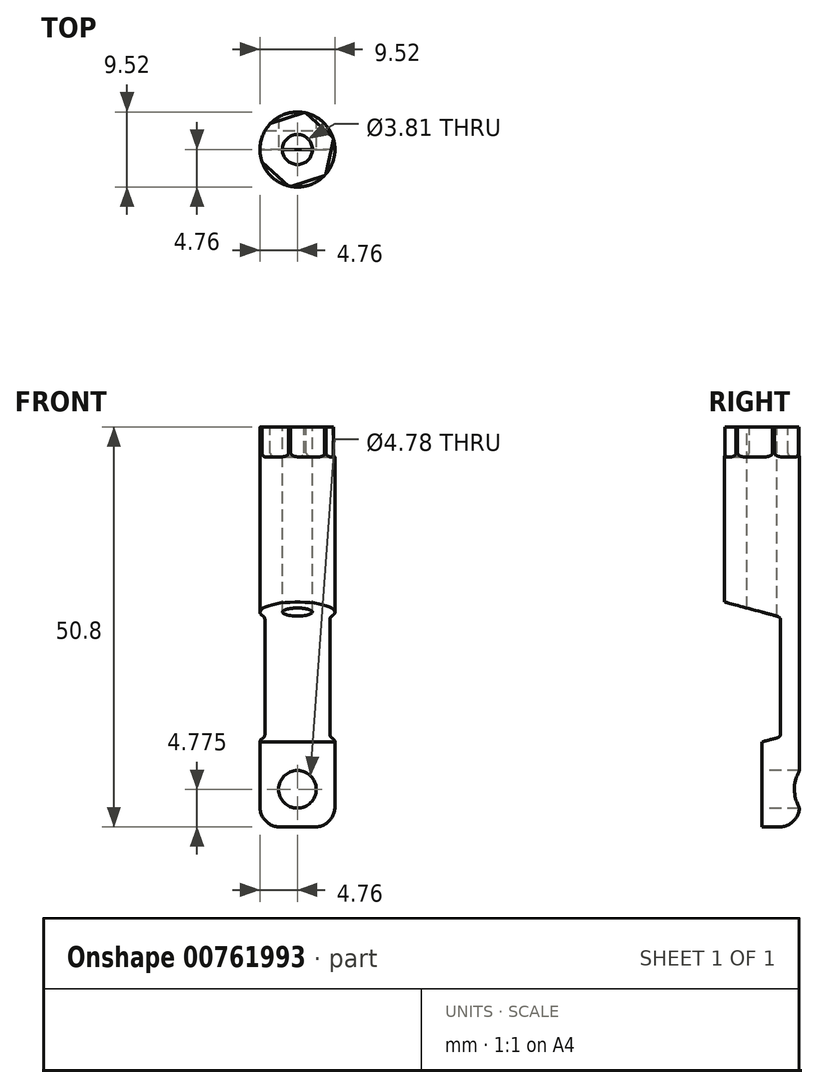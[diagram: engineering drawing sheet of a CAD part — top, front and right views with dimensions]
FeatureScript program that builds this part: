
annotation { "Feature Type Name" : "Feature", "Feature Type Description" : "" }
export const myFeature = defineFeature(function(context is Context, id is Id, definition is map)
    precondition{}
    {
        {
            var Q0;
            Q0=qCreatedBy(makeId("Top.planeOp"),FACE);
            var sketch = newSketch(context, id + "F0", { "sketchPlane" : qUnion([Q0])});
            skCircle(sketch, "E0", {"center": v(0, 0) * mm, "radius": 4.76 * mm});
            skSolve(sketch);
        }
        {
            var Q0;
            Q0=makeQuery(id+"F0.imprint","IMPRINT",FACE,{"disambiguationData":[TD([[makeQuery(id+"F0.imprint","IMPRINT",EDGE,{"derivedFrom":sQuery(id+"F0.wireOp",EDGE,"E0")}),1.0]])]});
            extrude(context, id + "F1", {"entities" : qUnion([Q0]), "depth" : 50.8 * mm, "offsetDistance" : 25.4 * mm});
        }
        {
            var Q0;
            Q0=qCreatedBy(makeId("Front.planeOp"),FACE);
            cPlane(context, id + "F2", {"entities" : qUnion([Q0]), "cplaneType" : CPlaneType.OFFSET, "offset" : 4.76 * mm, "width" : 152.4 * mm, "height" : 152.4 * mm});
        }
        {
            var Q0;
            Q0=qCreatedBy(id+"F2.planeOp",FACE);
            var sketch = newSketch(context, id + "F3", { "sketchPlane" : qUnion([Q0])});
            skLineSegment(sketch, "E1.bottom", {"start": v(-7.62, 9.53) * mm, "end": v(7.62, 9.53) * mm});
            skLineSegment(sketch, "E1.top", {"start": v(-7.62, 28.57) * mm, "end": v(7.62, 28.57) * mm});
            skLineSegment(sketch, "E1.left", {"start": v(-7.62, 9.53) * mm, "end": v(-7.62, 28.57) * mm});
            skLineSegment(sketch, "E1.right", {"start": v(7.62, 9.53) * mm, "end": v(7.62, 28.57) * mm});
            skSolve(sketch);
        }
        {
            var Q0;
            Q0 = qSketchRegion(id + "F3", true);
            extrude(context, id + "F4", {"entities" : qUnion([Q0]), "operationType" : NewBodyOperationType.REMOVE, "oppositeDirection" : true, "depth" : 7.14 * mm, "offsetDistance" : 25.4 * mm, "hasDraft" : true, "draftAngle" : 15 * degree, "draftPullDirection" : true});
        }
        {
            var Q0;
            Q0=qCreatedBy(id+"F2.planeOp",FACE);
            var sketch = newSketch(context, id + "F5", { "sketchPlane" : qUnion([Q0])});
            skLineSegment(sketch, "E2.bottom", {"start": v(-8.92, 12.6) * mm, "end": v(11.04, 12.6) * mm});
            skLineSegment(sketch, "E2.top", {"start": v(-8.92, -5.6) * mm, "end": v(11.04, -5.6) * mm});
            skLineSegment(sketch, "E2.left", {"start": v(-8.92, 12.6) * mm, "end": v(-8.92, -5.6) * mm});
            skLineSegment(sketch, "E2.right", {"start": v(11.04, 12.6) * mm, "end": v(11.04, -5.6) * mm});
            skSolve(sketch);
        }
        {
            var Q0;
            Q0 = qSketchRegion(id + "F5", true);
            extrude(context, id + "F6", {"entities" : qUnion([Q0]), "operationType" : NewBodyOperationType.REMOVE, "oppositeDirection" : true, "depth" : 4.78 * mm, "offsetDistance" : 25.4 * mm});
        }
        {
            var Q0;
            Q0=makeQuery(id+"F1.opExtrude","CAP_EDGE",EDGE,{"disambiguationData":[OSD([sQuery(id+"F0.wireOp",EDGE,"E0")])],"isStart":true});
            fillet(context, id + "F7", {"entities" : qUnion([Q0]), "radius" : 2.54 * mm, "tangentPropagation" : true, "allowEdgeOverflow" : false});
        }
        {
            var Q0;
            Q0=makeQuery(id+"F6.boolean.opBoolean","COPY",FACE,{"derivedFrom":makeQuery(id+"F6.opExtrude","CAP_FACE",FACE,{"disambiguationData":[OSD([sQuery(id+"F5.wireOp",EDGE,"E2.bottom"),sQuery(id+"F5.wireOp",EDGE,"E2.top"),sQuery(id+"F5.wireOp",EDGE,"E2.left"),sQuery(id+"F5.wireOp",EDGE,"E2.right")])],"isStart":false})});
            var sketch = newSketch(context, id + "F8", { "sketchPlane" : qUnion([Q0])});
            skCircle(sketch, "E3", {"center": v(0, 4.78) * mm, "radius": 2.39 * mm});
            skSolve(sketch);
        }
        {
            var Q0;
            Q0=makeQuery(id+"F8.imprint","IMPRINT",FACE,{"disambiguationData":[TD([[makeQuery(id+"F8.imprint","IMPRINT",EDGE,{"derivedFrom":sQuery(id+"F8.wireOp",EDGE,"E3")}),1.0]])]});
            extrude(context, id + "F9", {"entities" : qUnion([Q0]), "operationType" : NewBodyOperationType.REMOVE, "oppositeDirection" : true, "depth" : 25.4 * mm, "offsetDistance" : 25.4 * mm});
        }
        {
            var Q0;
            Q0=makeQuery(id+"F1.opExtrude","CAP_FACE",FACE,{"disambiguationData":[OSD([sQuery(id+"F0.wireOp",EDGE,"E0")])],"isStart":false});
            var sketch = newSketch(context, id + "F10", { "sketchPlane" : qUnion([Q0])});
            skCircle(sketch, "E4", {"center": v(0, 0) * mm, "radius": 1.9 * mm});
            skSolve(sketch);
        }
        {
            var Q0;
            Q0 = qSketchRegion(id + "F10", true);
            extrude(context, id + "F11", {"entities" : qUnion([Q0]), "operationType" : NewBodyOperationType.REMOVE, "oppositeDirection" : true, "depth" : 25.4 * mm, "offsetDistance" : 25.4 * mm});
        }
        {
            var Q0;
            Q0=makeQuery(id+"F1.opExtrude","CAP_FACE",FACE,{"disambiguationData":[OSD([sQuery(id+"F0.wireOp",EDGE,"E0")])],"isStart":false});
            var sketch = newSketch(context, id + "F12", { "sketchPlane" : qUnion([Q0])});
            skCircle(sketch, "E5.cCircle", {"center": v(0, 0) * mm, "radius": 4.84 * mm, "construction": true});
            skLineSegment(sketch, "E5.0", {"start": v(3.6, -3.23) * mm, "end": v(-1, -4.73) * mm});
            skLineSegment(sketch, "E5.1", {"start": v(-1, -4.73) * mm, "end": v(-4.6, -1.5) * mm});
            skLineSegment(sketch, "E5.2", {"start": v(-4.6, -1.5) * mm, "end": v(-3.63, 3.08) * mm});
            skLineSegment(sketch, "E5.3", {"start": v(-3.6, 3.23) * mm, "end": v(1, 4.73) * mm});
            skLineSegment(sketch, "E5.4", {"start": v(1, 4.73) * mm, "end": v(4.6, 1.5) * mm});
            skLineSegment(sketch, "E5.5", {"start": v(4.6, 1.5) * mm, "end": v(3.6, -3.23) * mm});
            skLineSegment(sketch, "E6", {"start": v(-4.6, -1.5) * mm, "end": v(-3.6, 3.23) * mm});
            skSolve(sketch);
        }
        {
            var Q0;
            {var subQ0=sQuery(id+"F12.wireOp",EDGE,"E6");var subQ1=makeQuery(id+"F12.imprint","IMPRINT",VERTEX,{"derivedFrom":subQ0});Q0=makeQuery(id+"F12.imprint","IMPRINT",FACE,{"disambiguationData":[TD([[makeQuery(id+"F12.imprint","IMPRINT",EDGE,{"disambiguationData":[TD([[subQ1,1.0]])],"derivedFrom":subQ0}),1.0]])]});}
            var Q1;
            {var subQ0=sQuery(id+"F12.wireOp",EDGE,"E5.1");var subQ1=makeQuery(id+"F1.opExtrude","CAP_EDGE",EDGE,{"disambiguationData":[OSD([sQuery(id+"F0.wireOp",EDGE,"E0")])],"isStart":false});var subQ2=makeQuery(id+"F12.imprint","INTERSECT",VERTEX,{"disambiguationData":[OD(0.0)],"derivedFrom":[subQ1,subQ0]});Q1=makeQuery(id+"F12.imprint","IMPRINT",FACE,{"disambiguationData":[TD([[makeQuery(id+"F12.imprint","IMPRINT",EDGE,{"disambiguationData":[TD([[subQ2,-1.0]])],"derivedFrom":subQ0}),1.0]])]});}
            var Q2;
            {var subQ0=sQuery(id+"F12.wireOp",EDGE,"E5.3");var subQ1=makeQuery(id+"F1.opExtrude","CAP_EDGE",EDGE,{"disambiguationData":[OSD([sQuery(id+"F0.wireOp",EDGE,"E0")])],"isStart":false});var subQ2=makeQuery(id+"F12.imprint","INTERSECT",VERTEX,{"disambiguationData":[OD(0.0)],"derivedFrom":[subQ1,subQ0]});Q2=makeQuery(id+"F12.imprint","IMPRINT",FACE,{"disambiguationData":[TD([[makeQuery(id+"F12.imprint","IMPRINT",EDGE,{"disambiguationData":[TD([[subQ2,-1.0]])],"derivedFrom":subQ0}),1.0]])]});}
            var Q3;
            {var subQ0=sQuery(id+"F12.wireOp",EDGE,"E5.4");var subQ1=makeQuery(id+"F1.opExtrude","CAP_EDGE",EDGE,{"disambiguationData":[OSD([sQuery(id+"F0.wireOp",EDGE,"E0")])],"isStart":false});var subQ2=makeQuery(id+"F12.imprint","INTERSECT",VERTEX,{"disambiguationData":[OD(0.0)],"derivedFrom":[subQ1,subQ0]});Q3=makeQuery(id+"F12.imprint","IMPRINT",FACE,{"disambiguationData":[TD([[makeQuery(id+"F12.imprint","IMPRINT",EDGE,{"disambiguationData":[TD([[subQ2,-1.0]])],"derivedFrom":subQ0}),1.0]])]});}
            var Q4;
            {var subQ0=sQuery(id+"F12.wireOp",EDGE,"E5.5");var subQ1=makeQuery(id+"F1.opExtrude","CAP_EDGE",EDGE,{"disambiguationData":[OSD([sQuery(id+"F0.wireOp",EDGE,"E0")])],"isStart":false});var subQ2=makeQuery(id+"F12.imprint","INTERSECT",VERTEX,{"disambiguationData":[OD(0.0)],"derivedFrom":[subQ1,subQ0]});Q4=makeQuery(id+"F12.imprint","IMPRINT",FACE,{"disambiguationData":[TD([[makeQuery(id+"F12.imprint","IMPRINT",EDGE,{"disambiguationData":[TD([[subQ2,-1.0]])],"derivedFrom":subQ0}),1.0]])]});}
            var Q5;
            {var subQ0=sQuery(id+"F12.wireOp",EDGE,"E5.0");var subQ1=makeQuery(id+"F1.opExtrude","CAP_EDGE",EDGE,{"disambiguationData":[OSD([sQuery(id+"F0.wireOp",EDGE,"E0")])],"isStart":false});var subQ2=makeQuery(id+"F12.imprint","INTERSECT",VERTEX,{"disambiguationData":[OD(0.0)],"derivedFrom":[subQ1,subQ0]});Q5=makeQuery(id+"F12.imprint","IMPRINT",FACE,{"disambiguationData":[TD([[makeQuery(id+"F12.imprint","IMPRINT",EDGE,{"disambiguationData":[TD([[subQ2,-1.0]])],"derivedFrom":subQ0}),1.0]])]});}
            extrude(context, id + "F13", {"entities" : qUnion([Q0, Q1, Q2, Q3, Q4, Q5]), "operationType" : NewBodyOperationType.REMOVE, "oppositeDirection" : true, "depth" : 3.8 * mm, "offsetDistance" : 25.4 * mm});
        }
        {
            var Q0;
            Q0=makeQuery(id+"F13.boolean.opBoolean","COPY",EDGE,{"derivedFrom":makeQuery(id+"F13.opExtrude","CAP_EDGE",EDGE,{"disambiguationData":[OSD([sQuery(id+"F12.wireOp",EDGE,"E6")])],"isStart":false})});
            var Q1;
            Q1=makeQuery(id+"F13.boolean.opBoolean","COPY",EDGE,{"derivedFrom":makeQuery(id+"F13.opExtrude","CAP_EDGE",EDGE,{"disambiguationData":[OSD([sQuery(id+"F12.wireOp",EDGE,"E5.1")])],"isStart":false})});
            var Q2;
            Q2=makeQuery(id+"F13.boolean.opBoolean","COPY",EDGE,{"derivedFrom":makeQuery(id+"F13.opExtrude","CAP_EDGE",EDGE,{"disambiguationData":[OSD([sQuery(id+"F12.wireOp",EDGE,"E5.0")])],"isStart":false})});
            var Q3;
            Q3=makeQuery(id+"F13.boolean.opBoolean","COPY",EDGE,{"derivedFrom":makeQuery(id+"F13.opExtrude","CAP_EDGE",EDGE,{"disambiguationData":[OSD([sQuery(id+"F12.wireOp",EDGE,"E5.5")])],"isStart":false})});
            var Q4;
            Q4=makeQuery(id+"F13.boolean.opBoolean","COPY",EDGE,{"derivedFrom":makeQuery(id+"F13.opExtrude","CAP_EDGE",EDGE,{"disambiguationData":[OSD([sQuery(id+"F12.wireOp",EDGE,"E5.4")])],"isStart":false})});
            var Q5;
            Q5=makeQuery(id+"F13.boolean.opBoolean","COPY",EDGE,{"derivedFrom":makeQuery(id+"F13.opExtrude","CAP_EDGE",EDGE,{"disambiguationData":[OSD([sQuery(id+"F12.wireOp",EDGE,"E5.3")])],"isStart":false})});
            var Q6;
            Q6=makeQuery(id+"F4.boolean.opBoolean","COPY",EDGE,{"derivedFrom":makeQuery(id+"F4.opExtrude","CAP_EDGE",EDGE,{"disambiguationData":[OSD([sQuery(id+"F3.wireOp",EDGE,"E1.top")])],"isStart":false})});
            var Q7;
            Q7=makeQuery(id+"F4.boolean.opBoolean","COPY",EDGE,{"derivedFrom":makeQuery(id+"F4.opExtrude","CAP_EDGE",EDGE,{"disambiguationData":[OSD([sQuery(id+"F3.wireOp",EDGE,"E1.bottom")])],"isStart":false})});
            fillet(context, id + "F14", {"entities" : qUnion([Q0, Q1, Q2, Q3, Q4, Q5, Q6, Q7]), "radius" : 0.5 * mm, "tangentPropagation" : true, "allowEdgeOverflow" : false});
        }
    });
